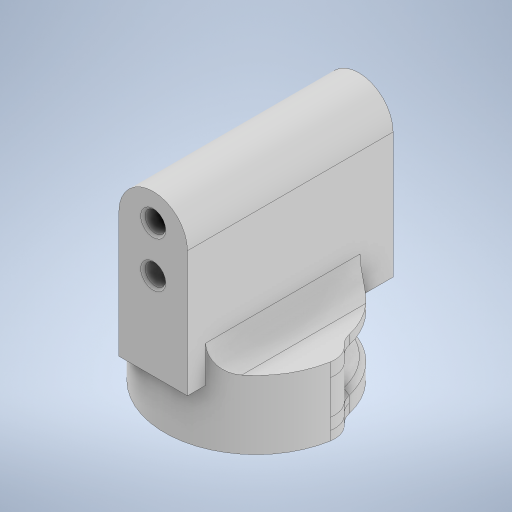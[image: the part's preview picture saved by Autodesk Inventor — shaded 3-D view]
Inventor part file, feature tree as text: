
AUTODESK INVENTOR PART (.ipt)
format: ipt  version: 2023 (Build 270158000, 158)  size: 457,216 bytes
history: native  units: mm
features: extrude x10, sketch x8, fillet x3, chamfer x2, other x1, projected_geometry x1
ambient origin geometry x8: Origin, YZ Plane, XZ Plane, XY Plane, X Axis, Y Axis, Z Axis, Center Point
bodies: Body1 (feature_tree)
feature tree (25):
  other  "솔리드1"
  extrude  "돌출1"  Depth=15.0mm
  extrude  "돌출2"  Depth=35.0mm
  fillet  "모깎기1"  Radius=45.0mm
  chamfer  "모따기1"  Distance=4.5mm
  sketch  "스케치3"
  extrude  "돌출3"  Depth=4.5mm
  extrude  "돌출5"  Depth=10.0mm
  extrude  "돌출6"  Depth=30.0mm TaperAngle=0.0deg
  fillet  "모깎기4"  Radius=7.5mm
  extrude  "돌출7"  Depth=0.5mm TaperAngle=45.0deg
  extrude  "돌출8"  Depth=40.0mm
  chamfer  "모따기2"  Distance=2.0mm
  fillet  "모깎기5"  Radius=3.0mm
  extrude  "돌출11"  Depth=10.0mm TaperAngle=0.0deg
  extrude  "돌출12"  Depth=7.5mm TaperAngle=0.0deg
  extrude  "돌출13"  Depth=3.0mm TaperAngle=0.0deg
  sketch  "스케치1"
  sketch  "스케치2"
  sketch  "스케치5"
  sketch  "스케치6"
  sketch  "스케치8"
  sketch  "스케치9"
  projected_geometry  "투영된 루프2"
  sketch  "스케치10"
